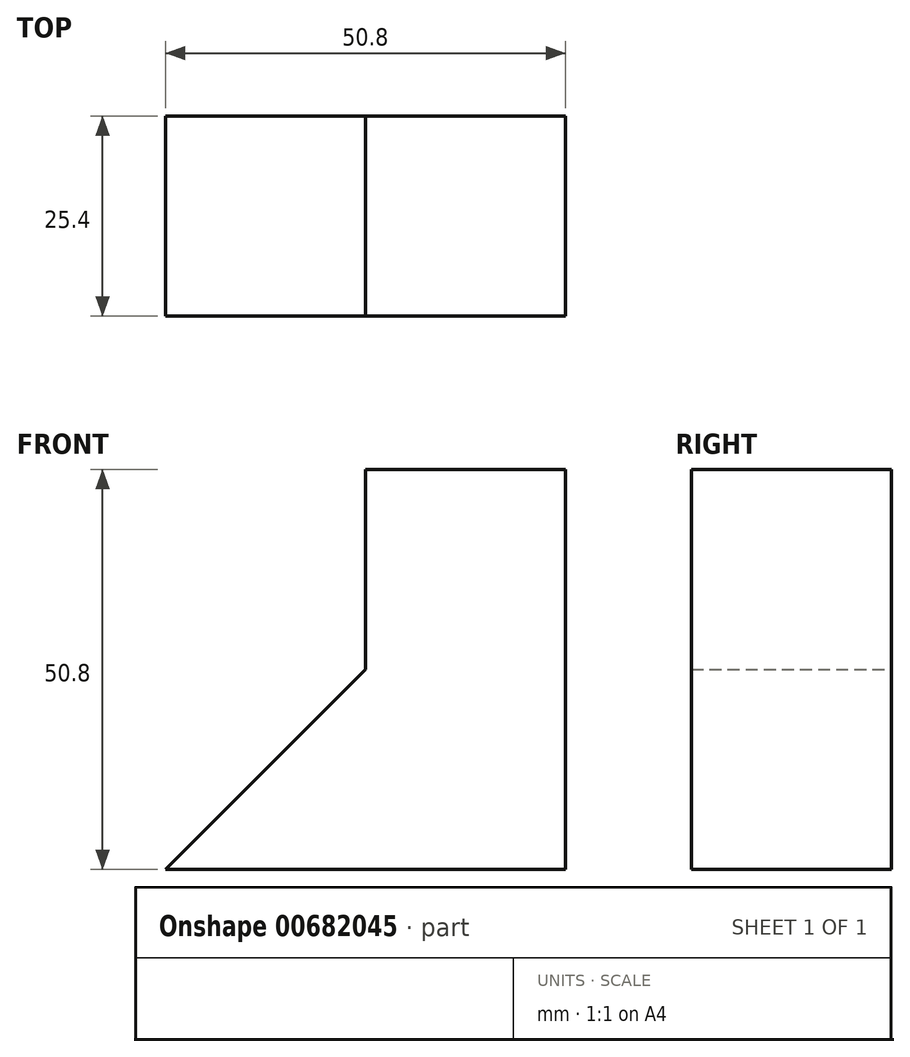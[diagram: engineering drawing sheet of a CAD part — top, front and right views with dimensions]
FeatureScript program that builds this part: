
annotation { "Feature Type Name" : "Feature", "Feature Type Description" : "" }
export const myFeature = defineFeature(function(context is Context, id is Id, definition is map)
    precondition{}
    {
        {
            var Q0;
            Q0=qCreatedBy(makeId("Front.planeOp"),FACE);
            var sketch = newSketch(context, id + "F0", { "sketchPlane" : qUnion([Q0])});
            skLineSegment(sketch, "E0", {"start": v(0, 0) * mm, "end": v(0, 50.8) * mm});
            skLineSegment(sketch, "E1", {"start": v(0, 0) * mm, "end": v(-50.8, 0) * mm});
            skLineSegment(sketch, "E2", {"start": v(0, 50.8) * mm, "end": v(-25.4, 50.8) * mm});
            skLineSegment(sketch, "E3", {"start": v(-25.4, 50.8) * mm, "end": v(-25.4, 25.4) * mm});
            skLineSegment(sketch, "E4", {"start": v(-25.4, 25.4) * mm, "end": v(-50.8, 0) * mm});
            skSolve(sketch);
        }
        {
            var Q0;
            Q0 = qSketchRegion(id + "F0", true);
            extrude(context, id + "F1", {"entities" : qUnion([Q0]), "depth" : 25.4 * mm, "offsetDistance" : 25.4 * mm});
        }
    });
